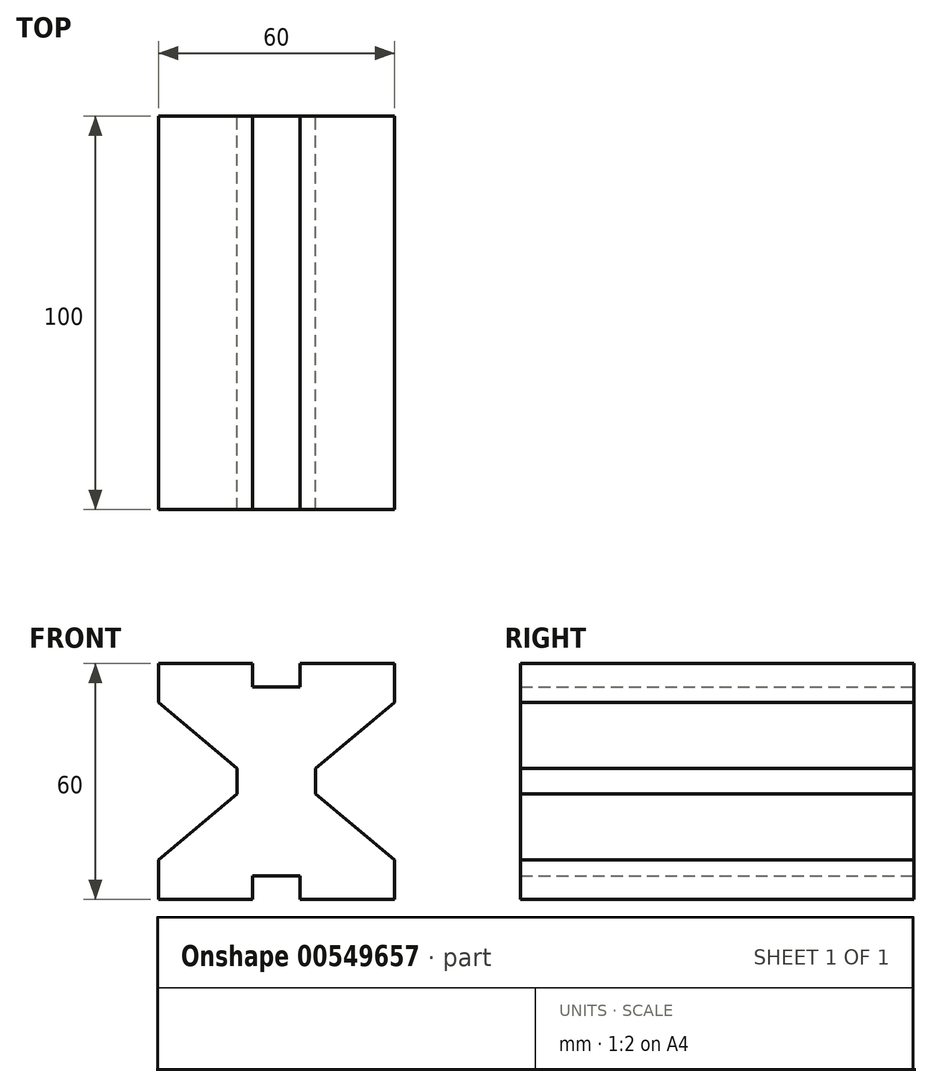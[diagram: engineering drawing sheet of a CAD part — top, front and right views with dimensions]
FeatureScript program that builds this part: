
annotation { "Feature Type Name" : "Feature", "Feature Type Description" : "" }
export const myFeature = defineFeature(function(context is Context, id is Id, definition is map)
    precondition{}
    {
        {
            var Q0;
            Q0=qCreatedBy(makeId("Front.planeOp"),FACE);
            var sketch = newSketch(context, id + "F0", { "sketchPlane" : qUnion([Q0])});
            skLineSegment(sketch, "E0", {"start": v(0, 0) * mm, "end": v(0, -50.2) * mm, "construction": true});
            skLineSegment(sketch, "E1", {"start": v(0, 0) * mm, "end": v(-28.48, 0) * mm, "construction": true});
            skLineSegment(sketch, "E2", {"start": v(-6, -24) * mm, "end": v(-6, -30) * mm});
            skLineSegment(sketch, "E3", {"start": v(-6, -30) * mm, "end": v(-30, -30) * mm});
            skLineSegment(sketch, "E4", {"start": v(-30, -30) * mm, "end": v(-30, -20) * mm});
            skLineSegment(sketch, "E5", {"start": v(-30, -20) * mm, "end": v(-10, -3.22) * mm});
            skLineSegment(sketch, "E6.MirrorCS", {"start": v(-30, 30) * mm, "end": v(-30, 20) * mm});
            skLineSegment(sketch, "E7.MirrorCS", {"start": v(-30, 20) * mm, "end": v(-10, 3.22) * mm});
            skLineSegment(sketch, "E8.MirrorCS", {"start": v(-6, 24) * mm, "end": v(-6, 30) * mm});
            skLineSegment(sketch, "E9.MirrorCS", {"start": v(-6, 30) * mm, "end": v(-30, 30) * mm});
            skLineSegment(sketch, "E10.MirrorCS", {"start": v(30, -30) * mm, "end": v(30, -20) * mm});
            skLineSegment(sketch, "E11.MirrorCS", {"start": v(6, -30) * mm, "end": v(30, -30) * mm});
            skLineSegment(sketch, "E12.MirrorCS", {"start": v(6, -24) * mm, "end": v(6, -30) * mm});
            skLineSegment(sketch, "E13.MirrorCS", {"start": v(30, -20) * mm, "end": v(10, -3.22) * mm});
            skLineSegment(sketch, "E14.MirrorCS", {"start": v(30, 30) * mm, "end": v(30, 20) * mm});
            skLineSegment(sketch, "E15.MirrorCS", {"start": v(6, 24) * mm, "end": v(6, 30) * mm});
            skLineSegment(sketch, "E16.MirrorCS", {"start": v(30, 20) * mm, "end": v(10, 3.22) * mm});
            skLineSegment(sketch, "E17.MirrorCS", {"start": v(6, 30) * mm, "end": v(30, 30) * mm});
            skLineSegment(sketch, "E18", {"start": v(-6, -24) * mm, "end": v(6, -24) * mm});
            skLineSegment(sketch, "E19", {"start": v(10, -3.22) * mm, "end": v(10, 3.22) * mm});
            skLineSegment(sketch, "E20", {"start": v(6, 24) * mm, "end": v(-6, 24) * mm});
            skLineSegment(sketch, "E21", {"start": v(-10, 3.22) * mm, "end": v(-10, -3.22) * mm});
            skSolve(sketch);
        }
        {
            var Q0;
            Q0 = qSketchRegion(id + "F0", true);
            extrude(context, id + "F1", {"entities" : qUnion([Q0]), "depth" : 100 * mm, "offsetDistance" : 25 * mm});
        }
    });
